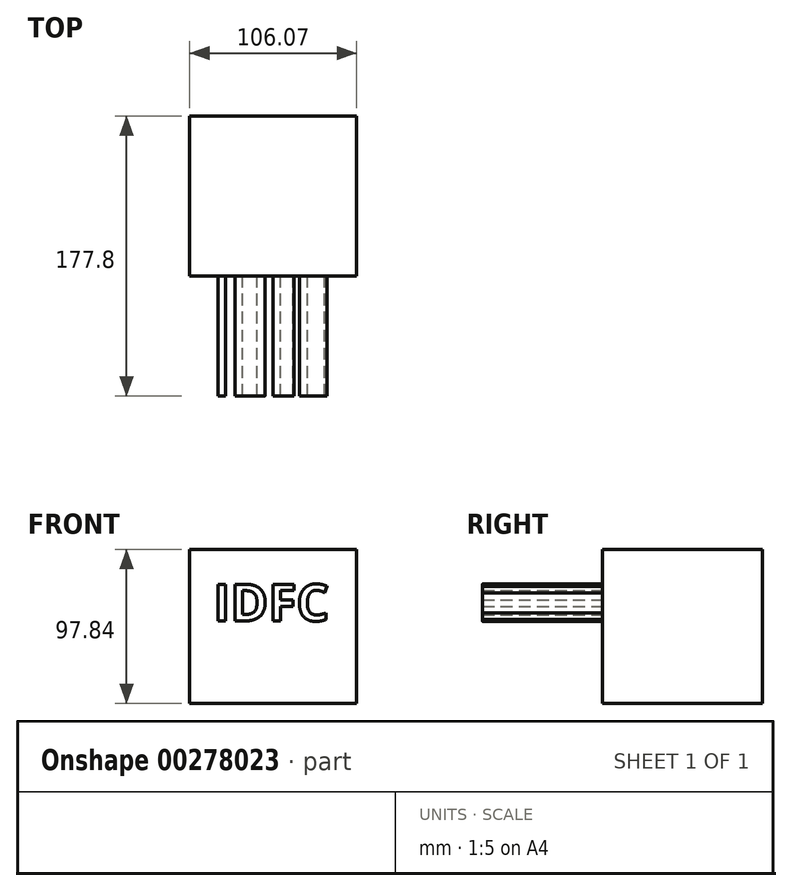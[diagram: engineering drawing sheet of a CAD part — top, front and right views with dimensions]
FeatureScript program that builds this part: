
annotation { "Feature Type Name" : "Feature", "Feature Type Description" : "" }
export const myFeature = defineFeature(function(context is Context, id is Id, definition is map)
    precondition{}
    {
        {
            var Q0;
            Q0=qCreatedBy(makeId("Front.planeOp"),FACE);
            var sketch = newSketch(context, id + "F0", { "sketchPlane" : qUnion([Q0])});
            skLineSegment(sketch, "E0.bottom", {"start": v(-49.99, 53.8) * mm, "end": v(56.08, 53.8) * mm});
            skLineSegment(sketch, "E0.top", {"start": v(-49.99, -44.04) * mm, "end": v(56.08, -44.04) * mm});
            skLineSegment(sketch, "E0.left", {"start": v(-49.99, 53.8) * mm, "end": v(-49.99, -44.04) * mm});
            skLineSegment(sketch, "E0.right", {"start": v(56.08, 53.8) * mm, "end": v(56.08, -44.04) * mm});
            skSolve(sketch);
        }
        {
            var Q0;
            Q0 = qSketchRegion(id + "F0", true);
            extrude(context, id + "F1", {"entities" : qUnion([Q0]), "depth" : 101.6 * mm});
        }
        {
            var Q0;
            Q0=makeQuery(id+"F1.opExtrude","CAP_FACE",FACE,{"disambiguationData":[OSD([sQuery(id+"F0.wireOp",EDGE,"E0.bottom"),sQuery(id+"F0.wireOp",EDGE,"E0.top"),sQuery(id+"F0.wireOp",EDGE,"E0.left"),sQuery(id+"F0.wireOp",EDGE,"E0.right")])],"isStart":false});
            var sketch = newSketch(context, id + "F2", { "sketchPlane" : qUnion([Q0])});
            skText(sketch, "E1", { "text": "IDFC", "fontName": "OpenSans-Bold.ttf"});
            const initialGuessF2  = {"E1": [-0.03505, 0.00838, 1, 0, 0.02347]};
            skSetInitialGuess(sketch, initialGuessF2);
            skSolve(sketch);
        }
        {
            var Q0;
            Q0 = qSketchRegion(id + "F2", true);
            extrude(context, id + "F3", {"entities" : qUnion([Q0]), "operationType" : NewBodyOperationType.ADD, "depth" : 76.2 * mm});
        }
    });
